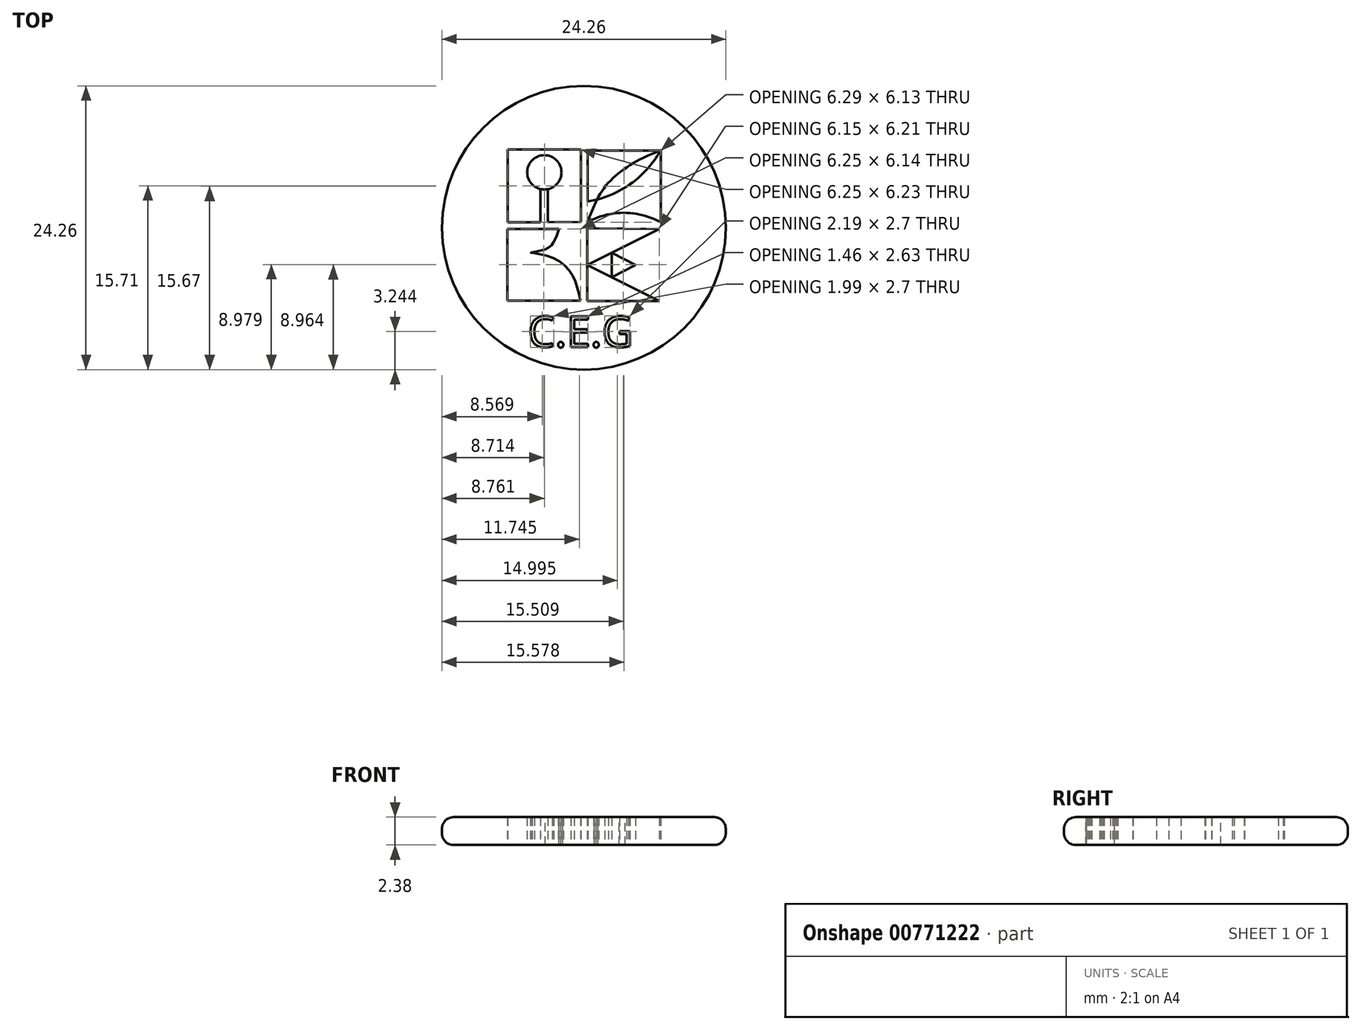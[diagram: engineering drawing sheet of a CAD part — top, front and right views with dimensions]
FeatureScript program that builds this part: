
annotation { "Feature Type Name" : "Feature", "Feature Type Description" : "" }
export const myFeature = defineFeature(function(context is Context, id is Id, definition is map)
    precondition{}
    {
        {
            var Q0;
            Q0=qCreatedBy(makeId("Top.planeOp"),FACE);
            var sketch = newSketch(context, id + "F0", { "sketchPlane" : qUnion([Q0])});
            skCircle(sketch, "E0", {"center": v(0, 0) * mm, "radius": 12.12 * mm});
            skLineSegment(sketch, "E1", {"start": v(-3.72, 0.47) * mm, "end": v(-6.5, 0.47) * mm});
            skLineSegment(sketch, "E2", {"start": v(-6.5, 0.47) * mm, "end": v(-6.5, 6.7) * mm});
            skLineSegment(sketch, "E3", {"start": v(-6.5, 6.7) * mm, "end": v(-0.25, 6.7) * mm});
            skLineSegment(sketch, "E4", {"start": v(-0.25, 6.7) * mm, "end": v(-0.25, 0.5) * mm});
            skLineSegment(sketch, "E5", {"start": v(-0.25, 0.5) * mm, "end": v(-3.09, 0.47) * mm});
            skLineSegment(sketch, "E6", {"start": v(-3.09, 0.47) * mm, "end": v(-3.09, 2.92) * mm});
            skLineSegment(sketch, "E7", {"start": v(-3.72, 2.92) * mm, "end": v(-3.72, 0.47) * mm});
            skCircle(sketch, "E8", {"center": v(-3.37, 4.73) * mm, "radius": 1.47 * mm});
            skPoint(sketch, "E8.first.point", {"position": v(-4.63, 5.49) * mm});
            skPoint(sketch, "E8.second.point", {"position": v(-2.04, 5.34) * mm});
            skPoint(sketch, "E8.third.point", {"position": v(-3.36, 3.27) * mm});
            skLineSegment(sketch, "E9", {"start": v(0.32, 6.6) * mm, "end": v(0.32, 2.26) * mm});
            skLineSegment(sketch, "E10", {"start": v(0.32, 2.26) * mm, "end": v(1.12, 2.4) * mm});
            skLineSegment(sketch, "E11", {"start": v(1.12, 2.4) * mm, "end": v(0.3, 0.5) * mm});
            skLineSegment(sketch, "E12", {"start": v(0.32, 6.6) * mm, "end": v(6.6, 6.6) * mm});
            skLineSegment(sketch, "E13", {"start": v(6.6, 6.6) * mm, "end": v(6.6, 0.48) * mm});
            skFitSpline(sketch, "E14", {"points": [v(6.6, 6.6) * mm, v(1.12, 2.4) * mm], "startDerivative": vector(-3.16, -4.99) * mm, "endDerivative": vector(-8.5, -2.23) * mm});
            skFitSpline(sketch, "E15", {"points": [v(6.6, 6.6) * mm, v(1.12, 2.4) * mm], "startDerivative": vector(-7.3, -2.58) * mm, "endDerivative": vector(-2.85, -5.83) * mm});
            skFitSpline(sketch, "E16", {"points": [v(0.3, 0.5) * mm, v(6.6, 0.48) * mm], "startDerivative": vector(6.68, 3.25) * mm, "endDerivative": vector(6, -3.03) * mm});
            skLineSegment(sketch, "E17", {"start": v(0.3, -0.05) * mm, "end": v(0.3, -6.25) * mm});
            skLineSegment(sketch, "E18", {"start": v(0.3, -6.25) * mm, "end": v(6.46, -6.25) * mm});
            skLineSegment(sketch, "E19", {"start": v(6.46, -6.25) * mm, "end": v(0.3, -3.19) * mm});
            skLineSegment(sketch, "E20", {"start": v(0.3, -3.19) * mm, "end": v(6.46, -0.1) * mm});
            skLineSegment(sketch, "E21", {"start": v(6.46, -0.1) * mm, "end": v(0.3, -0.05) * mm});
            skLineSegment(sketch, "E22", {"start": v(2.4, -2.14) * mm, "end": v(2.4, -4.23) * mm});
            skLineSegment(sketch, "E23", {"start": v(2.4, -4.23) * mm, "end": v(4.42, -3.19) * mm});
            skLineSegment(sketch, "E24", {"start": v(4.42, -3.19) * mm, "end": v(2.4, -2.14) * mm});
            skLineSegment(sketch, "E25", {"start": v(-2.12, -0.1) * mm, "end": v(-6.54, -0.1) * mm});
            skLineSegment(sketch, "E26", {"start": v(-6.54, -0.1) * mm, "end": v(-6.54, -6.24) * mm});
            skLineSegment(sketch, "E27", {"start": v(-6.54, -6.24) * mm, "end": v(-0.3, -6.24) * mm});
            skFitSpline(sketch, "E28", {"points": [v(-2.12, -0.1) * mm, v(-2.36, -0.8) * mm, v(-2.79, -1.53) * mm, v(-3.59, -1.93) * mm, v(-4.53, -2.13) * mm, v(-3.26, -2.35) * mm, v(-1.12, -3.83) * mm, v(-0.3, -6.24) * mm], "startDerivative": vector(-2, -6.51) * mm, "endDerivative": vector(2.66, -12.96) * mm});
            skLineSegment(sketch, "E29", {"start": v(-3.72, 2.92) * mm, "end": v(-3.72, 3.3) * mm});
            skLineSegment(sketch, "E30", {"start": v(-3.09, 2.92) * mm, "end": v(-3.09, 3.3) * mm});
            skText(sketch, "E31", { "text": "C.E.G", "fontName": "OpenSans-Regular.ttf"});
            const initialGuessF0  = {"E31": [-0.00478, -0.0102, 1, 0, 0.00265]};
            skSetInitialGuess(sketch, initialGuessF0);
            skSolve(sketch);
        }
        {
            var Q0;
            Q0=makeQuery(id+"F0.imprint","IMPRINT",FACE,{"disambiguationData":[TD([[makeQuery(id+"F0.imprint","IMPRINT",EDGE,{"derivedFrom":sQuery(id+"F0.wireOp",EDGE,"E0")}),1.0]])]});
            extrude(context, id + "F1", {"entities" : qUnion([Q0]), "depth" : 2.38 * mm, "offsetDistance" : 25 * mm});
        }
        {
            var Q0;
            Q0=makeQuery(id+"F1.opExtrude","CAP_EDGE",EDGE,{"disambiguationData":[OSD([sQuery(id+"F0.wireOp",EDGE,"E0")])],"isStart":false});
            var Q1;
            Q1=makeQuery(id+"F1.opExtrude","CAP_EDGE",EDGE,{"disambiguationData":[OSD([sQuery(id+"F0.wireOp",EDGE,"E0")])],"isStart":true});
            fillet(context, id + "F2", {"entities" : qUnion([Q0, Q1]), "radius" : 1 * mm, "tangentPropagation" : true, "allowEdgeOverflow" : false});
        }
        {
            var Q0;
            Q0=makeQuery(id+"F0.imprint","IMPRINT",FACE,{"disambiguationData":[TD([[makeQuery(id+"F0.imprint","IMPRINT",EDGE,{"derivedFrom":sQuery(id+"F0.wireOp",EDGE,"E8")}),1.0]])]});
            extrude(context, id + "F3", {"entities" : qUnion([Q0]), "depth" : 2.38 * mm, "offsetDistance" : 25 * mm});
        }
        {
            var Q0;
            Q0=makeQuery(id+"F0.imprint","IMPRINT",FACE,{"disambiguationData":[TD([[makeQuery(id+"F0.imprint","IMPRINT",EDGE,{"derivedFrom":sQuery(id+"F0.wireOp",EDGE,"E14")}),-1.0]])]});
            var Q1;
            {var subQ3=sQuery(id+"F0.wireOp",EDGE,"E22");Q1=makeQuery(id+"F0.imprint","IMPRINT",FACE,{"disambiguationData":[TD([[makeQuery(id+"F0.imprint","IMPRINT",EDGE,{"derivedFrom":subQ3}),-1.0]])]});}
            extrude(context, id + "F4", {"entities" : qUnion([Q0, Q1]), "operationType" : NewBodyOperationType.ADD, "depth" : 2.38 * mm, "offsetDistance" : 25 * mm});
        }
    });
